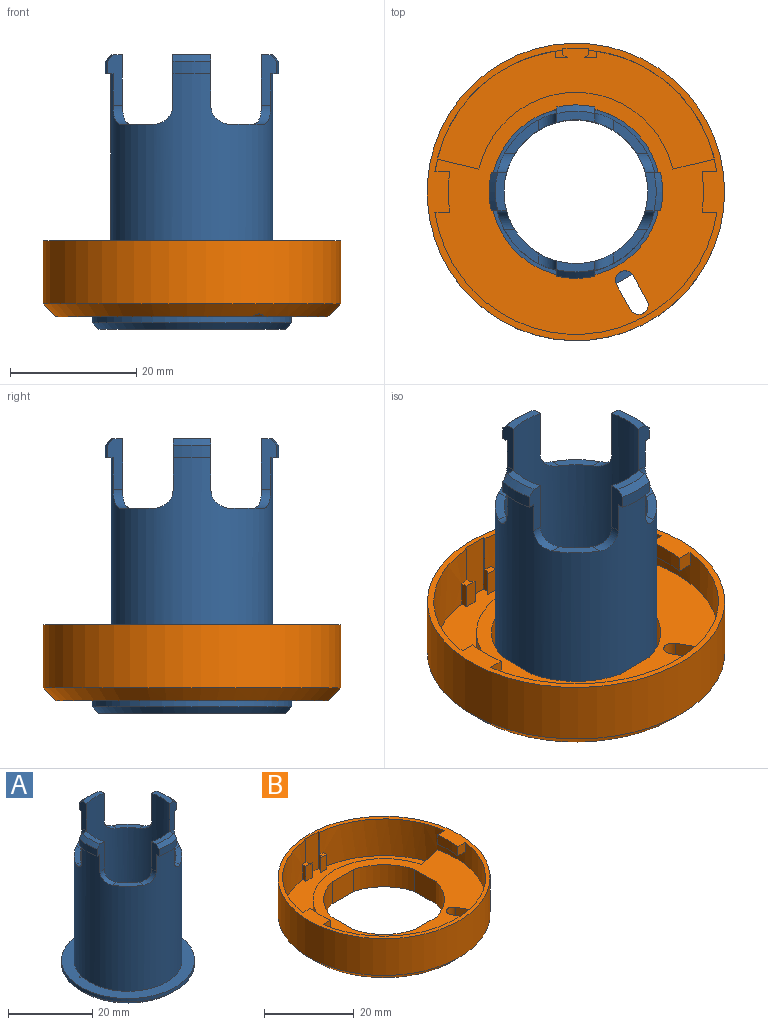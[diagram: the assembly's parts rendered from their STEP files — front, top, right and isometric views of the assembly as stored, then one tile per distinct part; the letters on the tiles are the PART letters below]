
ASSEMBLY  parts=2 mates=1
PART A: 48 faces, bbox 31.6x31.6x43.5 mm
  f0: cylinder r=11.4mm len=43.5mm, axis (0,0,-1), area 2611.4mm2, adj f4,f5,f6,f7,f9,f10,f12,f14
  f1: cylinder r=12.83mm len=38.5mm, axis (0,0,-1), area 2668.6mm2, adj f2,f4,f5,f7,f9,f11,f12,f14
  f2: plane 6x1.28mm, normal (0,0,-1), area 5.6mm2, adj f1,f3,f4,f5
  f3: cylinder r=13.75mm len=6mm, axis (0,0,-1), area 12.1mm2, adj f2,f4,f5,f44
  f4: plane 8.01x2.43mm, normal (-1,0,0), area 14.1mm2, adj f0,f1,f2,f3,f6,f40,f44
  f5: plane 8.01x2.43mm, normal (1,0,0), area 14.1mm2, adj f0,f1,f2,f3,f6,f38,f44
  f6: plane 6x1.75mm, normal (0,0,1), area 8.2mm2, adj f0,f4,f5,f44
  f7: plane 8.01x2.43mm, normal (0,1,0), area 14.1mm2, adj f0,f1,f8,f10,f11,f39,f47
  f8: cylinder r=13.75mm len=6mm, axis (0,0,-1), area 12.1mm2, adj f7,f9,f11,f47
  f9: plane 8.01x2.43mm, normal (0,-1,0), area 14.1mm2, adj f0,f1,f8,f10,f11,f41,f47
  f10: plane 6x1.75mm, normal (0,0,1), area 8.2mm2, adj f0,f7,f9,f47
  f11: plane 6x1.28mm, normal (0,0,-1), area 5.6mm2, adj f1,f7,f8,f9
  f12: plane 8.01x2.43mm, normal (-1,0,0), area 14.1mm2, adj f0,f1,f13,f15,f16,f42,f46
  f13: cylinder r=13.75mm len=6mm, axis (0,0,-1), area 12.1mm2, adj f12,f14,f16,f46
  f14: plane 8.01x2.43mm, normal (1,0,0), area 14.1mm2, adj f0,f1,f13,f15,f16,f35,f46
  f15: plane 6x1.75mm, normal (0,0,1), area 8.2mm2, adj f0,f12,f14,f46
  f16: plane 6x1.28mm, normal (0,0,-1), area 5.6mm2, adj f1,f12,f13,f14
  f17: plane 8.01x2.43mm, normal (0,1,0), area 14.1mm2, adj f0,f1,f19,f20,f21,f37,f45
  f18: plane 8.01x2.43mm, normal (0,-1,0), area 14.1mm2, adj f0,f1,f19,f20,f21,f36,f45
  f19: cylinder r=13.75mm len=6mm, axis (0,0,-1), area 12.1mm2, adj f17,f18,f21,f45
  f20: plane 6x1.75mm, normal (0,0,1), area 8.2mm2, adj f0,f17,f18,f45
  f21: plane 6x1.28mm, normal (0,0,-1), area 5.6mm2, adj f1,f17,f18,f19
  f22: plane 5.34x5.34mm, normal (0,0,1), area 9.3mm2, adj f0,f1,f41,f42
  f23: plane 5.34x5.34mm, normal (0,0,1), area 9.3mm2, adj f0,f1,f39,f40
  f24: plane 5.34x5.34mm, normal (0,0,1), area 9.3mm2, adj f0,f1,f37,f38
  f25: plane 5.34x5.34mm, normal (0,0,1), area 9.3mm2, adj f0,f1,f35,f36
  f26: plane 2x0.06mm, normal (-0.23,0.97,0), area 0.1mm2, adj f27,f30,f33,f34
  f27: plane 2x0.27mm, normal (1,0,0), area 0.5mm2, adj f26,f30,f33,f34
  f28: plane 2x0.27mm, normal (-1,0,0), area 0.5mm2, adj f29,f31,f33,f34
  f29: plane 2x0.06mm, normal (0.23,0.97,0), area 0.1mm2, adj f28,f31,f33,f34
  f30: cylinder r=13.42mm len=2mm, axis (0,0,1), area 0.5mm2, adj f26,f27,f33,f34
  f31: cylinder r=13.42mm len=2mm, axis (0,0,1), area 0.5mm2, adj f28,f29,f33,f34
  f32: cylinder r=15.8mm len=31.6mm, axis (0,0,1), area 99.3mm2, adj f34,f43
  f33: plane 29.6x29.6mm, normal (0,0,-1), area 279.8mm2, adj f0,f26,f27,f28,f29,f30,f31,f43
  f34: plane 31.6x31.6mm, normal (0,0,1), area 267.1mm2, adj f1,f26,f27,f28,f29,f30,f31,f32
  f35: cylinder r=3mm len=3mm, axis (0,1,0), area 7.2mm2, adj f0,f1,f14,f25
  f36: cylinder r=3mm len=3mm, axis (1,0,0), area 7.2mm2, adj f0,f1,f18,f25
  f37: cylinder r=3mm len=3mm, axis (-1,0,0), area 7.2mm2, adj f0,f1,f17,f24
  f38: cylinder r=3mm len=3mm, axis (0,1,0), area 7.2mm2, adj f0,f1,f5,f24
  f39: cylinder r=3mm len=3mm, axis (-1,0,0), area 7.2mm2, adj f0,f1,f7,f23
  f40: cylinder r=3mm len=3mm, axis (0,-1,0), area 7.2mm2, adj f0,f1,f4,f23
  f41: cylinder r=3mm len=3mm, axis (1,0,0), area 7.2mm2, adj f0,f1,f9,f22
  f42: cylinder r=3mm len=3mm, axis (0,-1,0), area 7.2mm2, adj f0,f1,f12,f22
  f43: cone r=15.8mm half-angle=45deg, axis (0,0,1), area 136mm2, adj f32,f33
  f44: cone r=12.75mm half-angle=45deg, axis (0,0,-1), area 8.6mm2, adj f3,f4,f5,f6
  f45: cone r=12.75mm half-angle=45deg, axis (0,0,-1), area 8.6mm2, adj f17,f18,f19,f20
  f46: cone r=12.75mm half-angle=45deg, axis (0,0,-1), area 8.6mm2, adj f12,f13,f14,f15
  f47: cone r=12.75mm half-angle=45deg, axis (0,0,-1), area 8.6mm2, adj f7,f8,f9,f10
PART B: 41 faces, bbox 47.2x47.2x12 mm
  f0: cylinder r=22.58mm len=45.15mm, axis (0,0,-1), area 1009.4mm2, adj f1,f4,f5,f16,f18,f21,f24,f25
  f1: plane 10x1mm, normal (1,0,0), area 6mm2, adj f0,f2,f5,f28,f29,f30
  f2: plane 10x4.12mm, normal (0,-1,0), area 41.2mm2, adj f1,f4,f5,f30
  f3: cylinder r=23.57mm len=47.15mm, axis (0,0,-1), area 1481.3mm2, adj f5,f40
  f4: plane 10x1mm, normal (-1,0,0), area 6mm2, adj f0,f2,f5,f22,f25,f30
  f5: plane 47.15x47.15mm, normal (0,0,1), area 173.7mm2, adj f0,f1,f2,f3,f4,f32,f33,f34
  f6: plane 6x3.93mm, normal (0.87,0.49,0), area 27mm2, adj f7,f20,f21,f31
  f7: cylinder r=1.5mm len=6mm, axis (0,0,-1), area 28.3mm2, adj f6,f8,f21,f31
  f8: plane 6x3.93mm, normal (-0.87,-0.49,0), area 27mm2, adj f7,f20,f21,f31
  f9: cylinder r=13.42mm len=9.65mm, axis (0,0,-1), area 85.9mm2, adj f10,f19,f21,f31
  f10: plane 6.7x6mm, normal (-1,0,0), area 40.2mm2, adj f9,f11,f21,f31
  f11: cylinder r=13.42mm len=9.65mm, axis (0,0,-1), area 85.9mm2, adj f10,f12,f21,f31
  f12: plane 6.7x6mm, normal (0,1,0), area 40.2mm2, adj f11,f13,f21,f31
  f13: cylinder r=13.42mm len=9.65mm, axis (0,0,-1), area 85.9mm2, adj f12,f14,f21,f31
  f14: plane 6.7x6mm, normal (1,0,0), area 40.2mm2, adj f13,f15,f21,f31
  f15: cylinder r=13.42mm len=9.65mm, axis (0,0,-1), area 85.9mm2, adj f14,f19,f21,f31
  f16: plane 6.59x4mm, normal (-0.23,0.97,0), area 27.1mm2, adj f0,f17,f21,f30
  f17: cylinder r=15.8mm len=30.75mm, axis (0,0,-1), area 169.2mm2, adj f16,f18,f21,f30
  f18: plane 6.59x4mm, normal (0.23,0.97,0), area 27.1mm2, adj f0,f17,f21,f30
  f19: plane 6.7x6mm, normal (0,-1,0), area 40.2mm2, adj f9,f15,f21,f31
  f20: cylinder r=1.5mm len=6mm, axis (0,0,-1), area 27.6mm2, adj f6,f8,f21,f31,f40
  f21: plane 45.15x38.38mm, normal (0,0,1), area 673.9mm2, adj f0,f6,f7,f8,f9,f10,f11,f12
  f22: plane 4x0.71mm, normal (-0.61,0.8,0), area 3.6mm2, adj f4,f23,f25,f30
  f23: plane 4x1.95mm, normal (0,-1,0), area 7.8mm2, adj f22,f24,f25,f30
  f24: plane 4x1.06mm, normal (1,0,0), area 4.2mm2, adj f0,f23,f25,f30
  f25: plane 1.95x1.21mm, normal (0,0,1), area 1.6mm2, adj f0,f4,f22,f23,f24
  f26: plane 4x1.06mm, normal (-1,0,0), area 4.2mm2, adj f0,f27,f29,f30
  f27: plane 4x1.95mm, normal (0,-1,0), area 7.8mm2, adj f26,f28,f29,f30
  f28: plane 4x0.71mm, normal (0.61,0.8,0), area 3.6mm2, adj f1,f27,f29,f30
  f29: plane 1.95x1.21mm, normal (0,0,1), area 1.6mm2, adj f0,f1,f26,f27,f28
  f30: plane 43.94x19.18mm, normal (0,0,1), area 345.9mm2, adj f0,f1,f2,f4,f16,f17,f18,f22
  f31: plane 43.15x43.15mm, normal (0,0,-1), area 883.8mm2, adj f6,f7,f8,f9,f10,f11,f12,f13
  f32: plane 2.5x2.35mm, normal (0,1,0), area 5.9mm2, adj f0,f5,f34,f35
  f33: plane 2.5x2.35mm, normal (0,-1,0), area 5.9mm2, adj f0,f5,f34,f35
  f34: cylinder r=20.25mm len=6.4mm, axis (0,0,-1), area 16.1mm2, adj f5,f32,f33,f35
  f35: plane 6.4x2.58mm, normal (0,0,-1), area 14.9mm2, adj f0,f32,f33,f34
  f36: plane 2.5x2.35mm, normal (0,-1,0), area 5.9mm2, adj f0,f5,f38,f39
  f37: plane 2.5x2.35mm, normal (0,1,0), area 5.9mm2, adj f0,f5,f38,f39
  f38: cylinder r=20.25mm len=6.4mm, axis (0,0,-1), area 16.1mm2, adj f5,f36,f37,f39
  f39: plane 6.4x2.58mm, normal (0,0,-1), area 14.9mm2, adj f0,f36,f37,f38
  f40: cone r=23.57mm half-angle=45deg, axis (0,0,1), area 400.3mm2, adj f3,f20,f31
PLACE A t=(-0.35,1.1,-4.56)mm
PLACE B t=(-0.35,1.1,-2.56)mm
MATE fastened A.f1 <-> B.f13  axis (0,0,-1) through (-0.35,1.1,-4.56)mm
